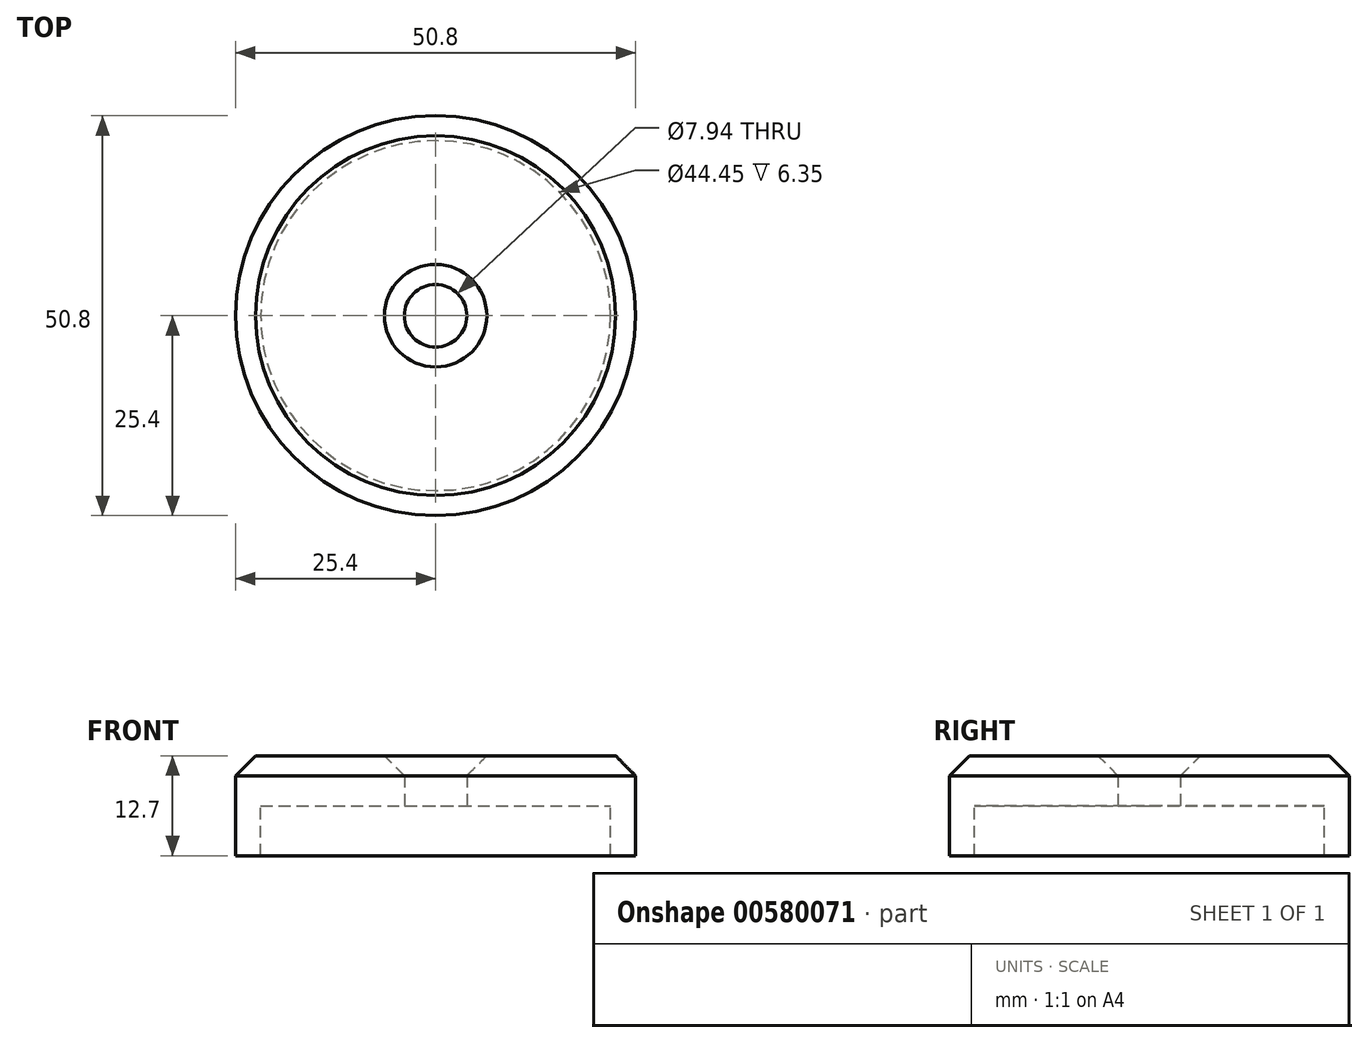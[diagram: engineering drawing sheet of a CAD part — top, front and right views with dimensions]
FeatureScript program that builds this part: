
annotation { "Feature Type Name" : "Feature", "Feature Type Description" : "" }
export const myFeature = defineFeature(function(context is Context, id is Id, definition is map)
    precondition{}
    {
        {
            var Q0;
            Q0=qCreatedBy(makeId("Top.planeOp"),FACE);
            var sketch = newSketch(context, id + "F0", { "sketchPlane" : qUnion([Q0])});
            skCircle(sketch, "E0", {"center": v(0, 0) * mm, "radius": 25.4 * mm});
            skSolve(sketch);
        }
        {
            var Q0;
            Q0 = qSketchRegion(id + "F0", true);
            extrude(context, id + "F1", {"entities" : qUnion([Q0]), "depth" : 6.35 * mm, "offsetDistance" : 25.4 * mm});
        }
        {
            var Q0;
            Q0=makeQuery(id+"F1.opExtrude","CAP_FACE",FACE,{"disambiguationData":[OSD([sQuery(id+"F0.wireOp",EDGE,"E0")])],"isStart":true});
            var sketch = newSketch(context, id + "F2", { "sketchPlane" : qUnion([Q0])});
            skCircle(sketch, "E1", {"center": v(0, 0) * mm, "radius": 25.4 * mm});
            skCircle(sketch, "E2", {"center": v(0, 0) * mm, "radius": 22.23 * mm});
            skCircle(sketch, "E3", {"center": v(0, 0) * mm, "radius": 3.97 * mm});
            skSolve(sketch);
        }
        {
            var Q0;
            Q0=makeQuery(id+"F2.imprint","IMPRINT",FACE,{"disambiguationData":[TD([[makeQuery(id+"F2.imprint","IMPRINT",EDGE,{"derivedFrom":sQuery(id+"F2.wireOp",EDGE,"E3")}),1.0]])]});
            extrude(context, id + "F3", {"entities" : qUnion([Q0]), "operationType" : NewBodyOperationType.REMOVE, "oppositeDirection" : true, "depth" : 25.4 * mm, "offsetDistance" : 25.4 * mm});
        }
        {
            var Q0;
            Q0=makeQuery(id+"F2.imprint","IMPRINT",FACE,{"disambiguationData":[TD([[makeQuery(id+"F2.imprint","IMPRINT",EDGE,{"derivedFrom":sQuery(id+"F2.wireOp",EDGE,"E1")}),-1.0]])]});
            extrude(context, id + "F4", {"entities" : qUnion([Q0]), "operationType" : NewBodyOperationType.ADD, "depth" : 6.35 * mm, "offsetDistance" : 25.4 * mm});
        }
        {
            var Q0;
            Q0=makeQuery(id+"F3.boolean.opBoolean","INTERSECT",EDGE,{"derivedFrom":[makeQuery(id+"F1.opExtrude","CAP_FACE",FACE,{"disambiguationData":[OSD([sQuery(id+"F0.wireOp",EDGE,"E0")])],"isStart":false}),makeQuery(id+"F3.opExtrude","SWEPT_FACE",FACE,{"disambiguationData":[OSD([sQuery(id+"F2.wireOp",EDGE,"E3")])]})]});
            var Q1;
            Q1=makeQuery(id+"F1.opExtrude","CAP_EDGE",EDGE,{"disambiguationData":[OSD([sQuery(id+"F0.wireOp",EDGE,"E0")])],"isStart":false});
            chamfer(context, id + "F5", {"entities" : qUnion([Q0, Q1]), "width" : 2.54 * mm, "tangentPropagation" : true});
        }
    });
